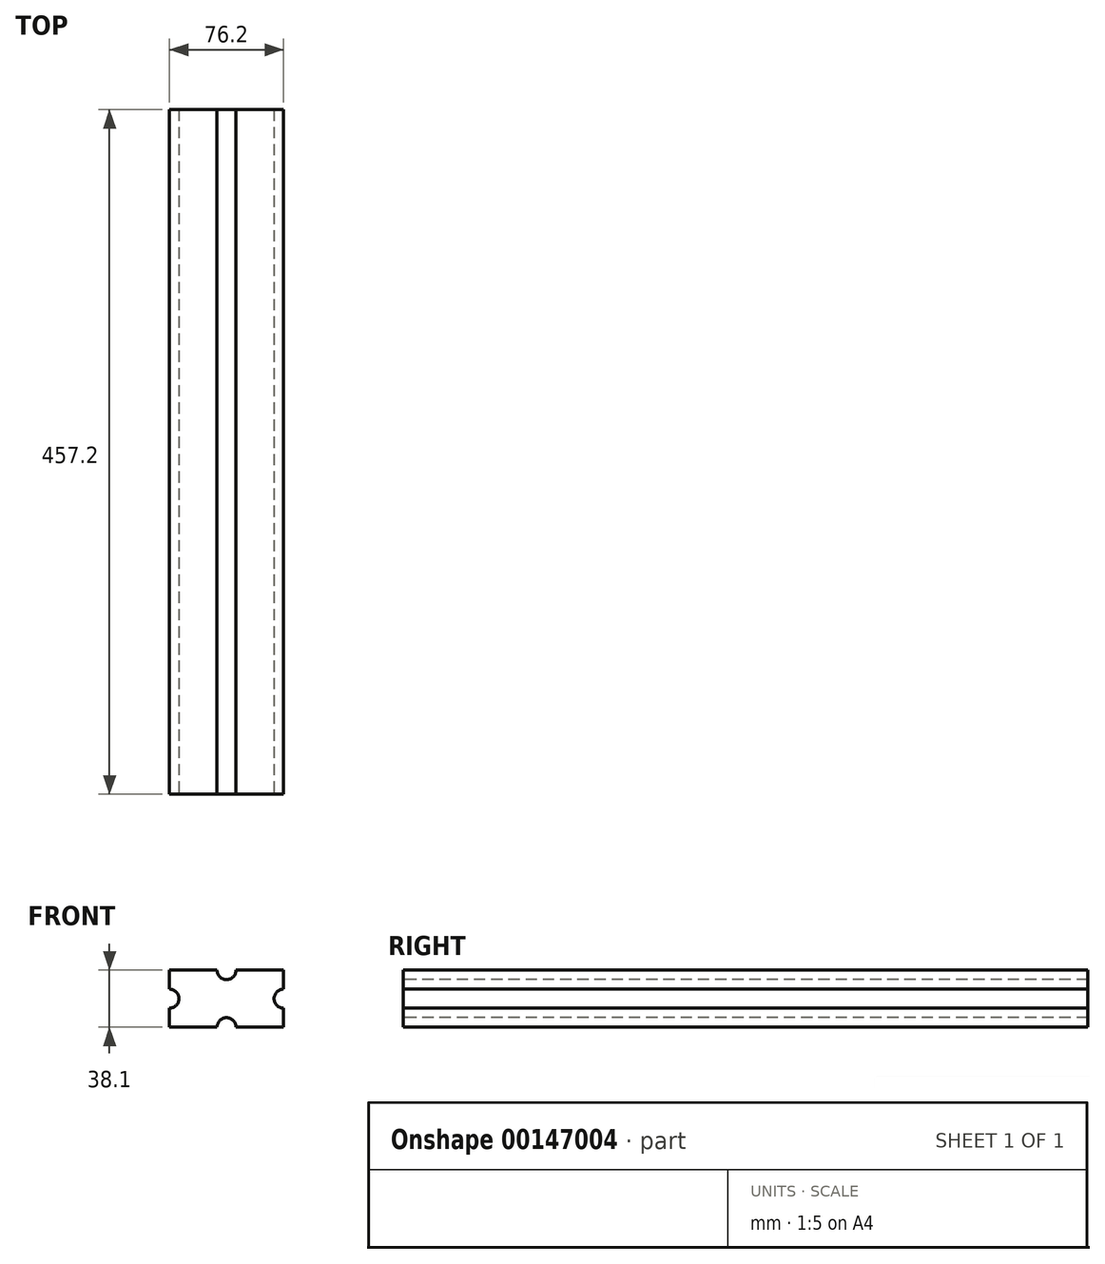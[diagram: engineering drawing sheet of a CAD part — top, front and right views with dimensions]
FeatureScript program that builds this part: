
annotation { "Feature Type Name" : "Feature", "Feature Type Description" : "" }
export const myFeature = defineFeature(function(context is Context, id is Id, definition is map)
    precondition{}
    {
        {
            var Q0;
            Q0=qCreatedBy(makeId("Front.planeOp"),FACE);
            var sketch = newSketch(context, id + "F0", { "sketchPlane" : qUnion([Q0])});
            skLineSegment(sketch, "E0.bottom", {"start": v(-85.3, 49.8) * mm, "end": v(-9.1, 49.8) * mm});
            skLineSegment(sketch, "E0.top", {"start": v(-85.3, 11.7) * mm, "end": v(-9.1, 11.7) * mm});
            skLineSegment(sketch, "E0.left", {"start": v(-85.3, 49.8) * mm, "end": v(-85.3, 11.7) * mm});
            skLineSegment(sketch, "E0.right", {"start": v(-9.1, 49.8) * mm, "end": v(-9.1, 11.7) * mm});
            skSolve(sketch);
        }
        {
            var Q0;
            Q0=makeQuery(id+"F0.imprint","IMPRINT",FACE,{"disambiguationData":[TD([[makeQuery(id+"F0.imprint","IMPRINT",EDGE,{"derivedFrom":sQuery(id+"F0.wireOp",EDGE,"E0.bottom")}),-1.0]])]});
            extrude(context, id + "F1", {"entities" : qUnion([Q0]), "depth" : 457.2 * mm});
        }
        {
            var Q0;
            Q0=makeQuery(id+"F1.opExtrude","CAP_FACE",FACE,{"disambiguationData":[OSD([sQuery(id+"F0.wireOp",EDGE,"E0.bottom"),sQuery(id+"F0.wireOp",EDGE,"E0.top"),sQuery(id+"F0.wireOp",EDGE,"E0.left"),sQuery(id+"F0.wireOp",EDGE,"E0.right")])],"isStart":false});
            var sketch = newSketch(context, id + "F2", { "sketchPlane" : qUnion([Q0])});
            skCircle(sketch, "E1", {"center": v(-47.2, 49.8) * mm, "radius": 6.35 * mm});
            skCircle(sketch, "E2", {"center": v(-9.1, 30.76) * mm, "radius": 6.35 * mm});
            skCircle(sketch, "E3", {"center": v(-47.2, 11.7) * mm, "radius": 6.35 * mm});
            skCircle(sketch, "E4", {"center": v(-85.3, 30.76) * mm, "radius": 6.35 * mm});
            skSolve(sketch);
        }
        {
            var Q0;
            Q0 = qSketchRegion(id + "F2", true);
            extrude(context, id + "F3", {"entities" : qUnion([Q0]), "operationType" : NewBodyOperationType.REMOVE, "oppositeDirection" : true, "depth" : 457.2 * mm});
        }
    });
